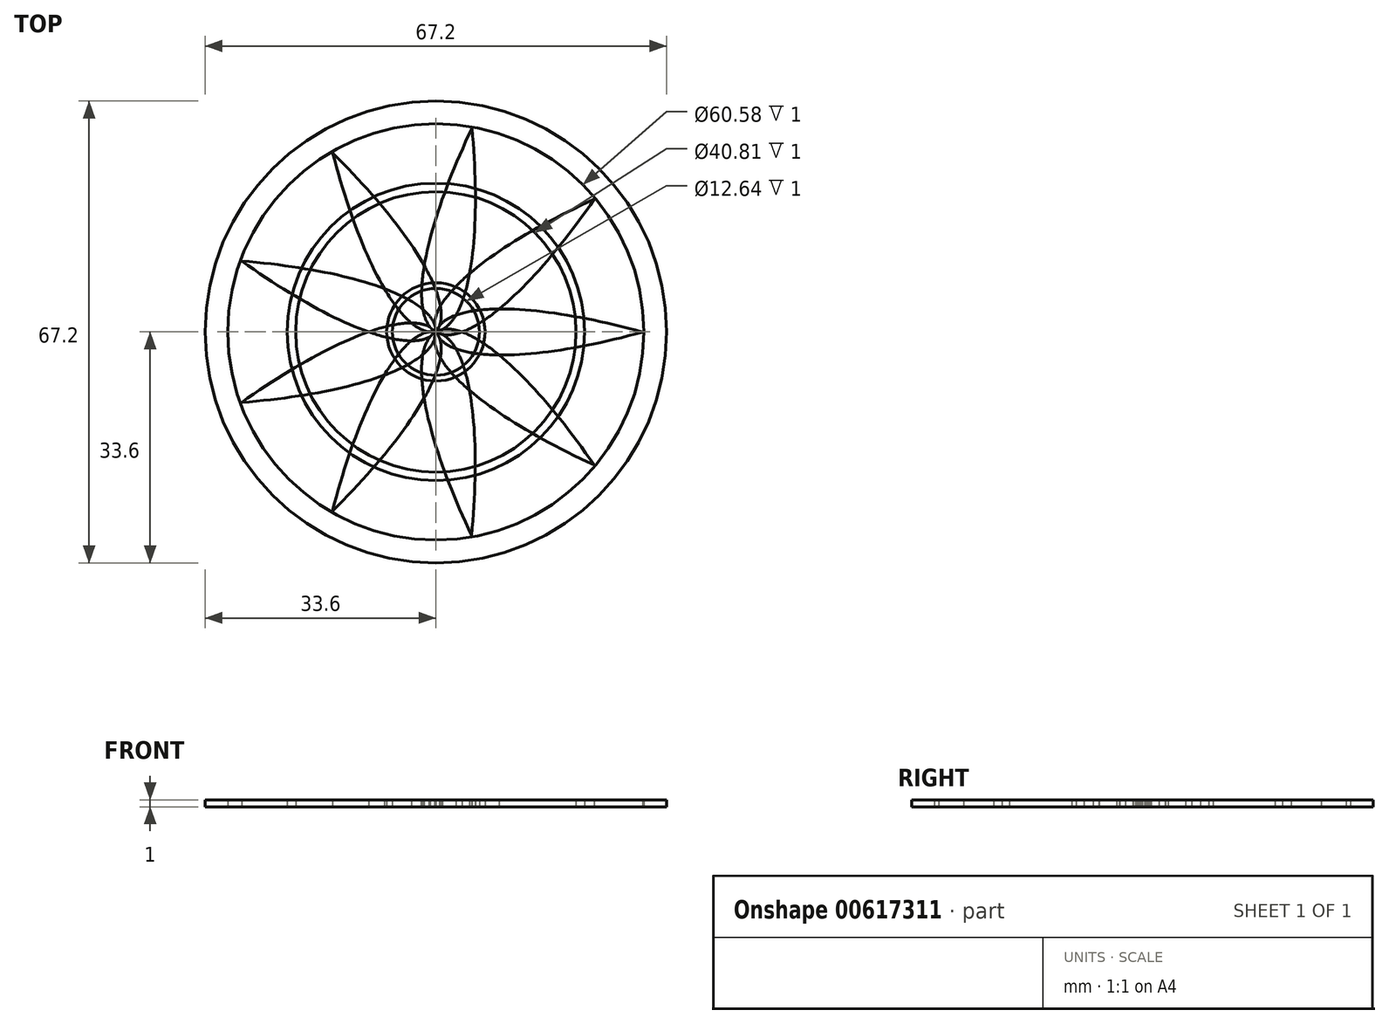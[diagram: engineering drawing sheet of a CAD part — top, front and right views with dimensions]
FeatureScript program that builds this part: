
annotation { "Feature Type Name" : "Feature", "Feature Type Description" : "" }
export const myFeature = defineFeature(function(context is Context, id is Id, definition is map)
    precondition{}
    {
        {
            var Q0;
            Q0=qCreatedBy(makeId("Top.planeOp"),FACE);
            var sketch = newSketch(context, id + "F0", { "sketchPlane" : qUnion([Q0])});
            skEllipse(sketch, "E0", {"center": v(-30.18, 25.36) * mm, "majorRadius": 39.42 * mm, "minorRadius": 10.73 * mm, "majorAxis": v(0.77, -0.64)});
            skEllipse(sketch, "E1.1.0", {"center": v(-39.42, 0.03) * mm, "majorRadius": 39.42 * mm, "minorRadius": 10.73 * mm, "majorAxis": v(1, 0)});
            skEllipse(sketch, "E1.2.0", {"center": v(-30.22, -25.31) * mm, "majorRadius": 39.42 * mm, "minorRadius": 10.73 * mm, "majorAxis": v(0.77, 0.64)});
            skEllipse(sketch, "E1.3.0", {"center": v(-6.88, -38.81) * mm, "majorRadius": 39.42 * mm, "minorRadius": 10.73 * mm, "majorAxis": v(0.17, 0.98)});
            skEllipse(sketch, "E1.4.0", {"center": v(19.68, -34.15) * mm, "majorRadius": 39.42 * mm, "minorRadius": 10.73 * mm, "majorAxis": v(-0.5, 0.87)});
            skEllipse(sketch, "E1.5.0", {"center": v(37.03, -13.51) * mm, "majorRadius": 39.42 * mm, "minorRadius": 10.73 * mm, "majorAxis": v(-0.94, 0.34)});
            skEllipse(sketch, "E1.6.0", {"center": v(37.05, 13.45) * mm, "majorRadius": 39.42 * mm, "minorRadius": 10.73 * mm, "majorAxis": v(-0.94, -0.34)});
            skEllipse(sketch, "E1.7.0", {"center": v(19.74, 34.12) * mm, "majorRadius": 39.42 * mm, "minorRadius": 10.73 * mm, "majorAxis": v(-0.5, -0.87)});
            skEllipse(sketch, "E1.8.0", {"center": v(-6.81, 38.82) * mm, "majorRadius": 39.42 * mm, "minorRadius": 10.73 * mm, "majorAxis": v(0.17, -0.98)});
            skPoint(sketch, "E1.center", {"position": v(0, 0) * mm});
            skSolve(sketch);
        }
        {
            var Q0;
            {var subQ0=sQuery(id+"F0.wireOp",EDGE,"E1.6.0");var subQ1=sQuery(id+"F0.wireOp",EDGE,"E1.1.0");var subQ2=makeQuery(id+"F0.imprint","INTERSECT",VERTEX,{"derivedFrom":[subQ1,subQ0]});Q0=makeQuery(id+"F0.imprint","IMPRINT",FACE,{"disambiguationData":[TD([[makeQuery(id+"F0.imprint","IMPRINT",EDGE,{"disambiguationData":[TD([[subQ2,-1.0]])],"derivedFrom":subQ1}),1.0]])]});}
            var Q1;
            {var subQ0=sQuery(id+"F0.wireOp",EDGE,"E1.5.0");var subQ1=sQuery(id+"F0.wireOp",EDGE,"E0");var subQ2=makeQuery(id+"F0.imprint","INTERSECT",VERTEX,{"derivedFrom":[subQ1,subQ0]});Q1=makeQuery(id+"F0.imprint","IMPRINT",FACE,{"disambiguationData":[TD([[makeQuery(id+"F0.imprint","IMPRINT",EDGE,{"disambiguationData":[TD([[subQ2,-1.0]])],"derivedFrom":subQ1}),1.0]])]});}
            var Q2;
            {var subQ0=sQuery(id+"F0.wireOp",EDGE,"E1.5.0");var subQ1=sQuery(id+"F0.wireOp",EDGE,"E0");var subQ2=makeQuery(id+"F0.imprint","INTERSECT",VERTEX,{"derivedFrom":[subQ1,subQ0]});Q2=makeQuery(id+"F0.imprint","IMPRINT",FACE,{"disambiguationData":[TD([[makeQuery(id+"F0.imprint","IMPRINT",EDGE,{"disambiguationData":[TD([[subQ2,1.0]])],"derivedFrom":subQ0}),1.0]])]});}
            var Q3;
            {var subQ0=sQuery(id+"F0.wireOp",EDGE,"E1.7.0");var subQ4=sQuery(id+"F0.wireOp",EDGE,"E1.4.0");var subQ6=makeQuery(id+"F0.imprint","INTERSECT",VERTEX,{"derivedFrom":[subQ4,subQ0]});Q3=makeQuery(id+"F0.imprint","IMPRINT",FACE,{"disambiguationData":[TD([[makeQuery(id+"F0.imprint","IMPRINT",EDGE,{"disambiguationData":[TD([[subQ6,-1.0]])],"derivedFrom":subQ4}),1.0]])]});}
            var Q4;
            {var subQ0=sQuery(id+"F0.wireOp",EDGE,"E1.6.0");var subQ4=sQuery(id+"F0.wireOp",EDGE,"E1.3.0");var subQ6=makeQuery(id+"F0.imprint","INTERSECT",VERTEX,{"derivedFrom":[subQ4,subQ0]});Q4=makeQuery(id+"F0.imprint","IMPRINT",FACE,{"disambiguationData":[TD([[makeQuery(id+"F0.imprint","IMPRINT",EDGE,{"disambiguationData":[TD([[subQ6,-1.0]])],"derivedFrom":subQ4}),1.0]])]});}
            var Q5;
            {var subQ0=sQuery(id+"F0.wireOp",EDGE,"E1.5.0");var subQ4=sQuery(id+"F0.wireOp",EDGE,"E1.2.0");var subQ6=makeQuery(id+"F0.imprint","INTERSECT",VERTEX,{"derivedFrom":[subQ4,subQ0]});Q5=makeQuery(id+"F0.imprint","IMPRINT",FACE,{"disambiguationData":[TD([[makeQuery(id+"F0.imprint","IMPRINT",EDGE,{"disambiguationData":[TD([[subQ6,-1.0]])],"derivedFrom":subQ4}),1.0]])]});}
            var Q6;
            {var subQ0=sQuery(id+"F0.wireOp",EDGE,"E1.4.0");var subQ4=sQuery(id+"F0.wireOp",EDGE,"E1.1.0");var subQ6=makeQuery(id+"F0.imprint","INTERSECT",VERTEX,{"derivedFrom":[subQ4,subQ0]});Q6=makeQuery(id+"F0.imprint","IMPRINT",FACE,{"disambiguationData":[TD([[makeQuery(id+"F0.imprint","IMPRINT",EDGE,{"disambiguationData":[TD([[subQ6,-1.0]])],"derivedFrom":subQ4}),1.0]])]});}
            var Q7;
            {var subQ0=sQuery(id+"F0.wireOp",EDGE,"E1.3.0");var subQ1=sQuery(id+"F0.wireOp",EDGE,"E0");var subQ2=makeQuery(id+"F0.imprint","INTERSECT",VERTEX,{"derivedFrom":[subQ1,subQ0]});Q7=makeQuery(id+"F0.imprint","IMPRINT",FACE,{"disambiguationData":[TD([[makeQuery(id+"F0.imprint","IMPRINT",EDGE,{"disambiguationData":[TD([[subQ2,-1.0]])],"derivedFrom":subQ1}),1.0]])]});}
            var Q8;
            {var subQ0=sQuery(id+"F0.wireOp",EDGE,"E1.7.0");var subQ1=sQuery(id+"F0.wireOp",EDGE,"E1.2.0");var subQ2=makeQuery(id+"F0.imprint","INTERSECT",VERTEX,{"derivedFrom":[subQ1,subQ0]});Q8=makeQuery(id+"F0.imprint","IMPRINT",FACE,{"disambiguationData":[TD([[makeQuery(id+"F0.imprint","IMPRINT",EDGE,{"disambiguationData":[TD([[subQ2,-1.0]])],"derivedFrom":subQ1}),1.0]])]});}
            extrude(context, id + "F1", {"entities" : qUnion([Q0, Q1, Q2, Q3, Q4, Q5, Q6, Q7, Q8]), "depth" : 1 * mm, "offsetDistance" : 25 * mm});
        }
        {
            var Q0;
            {var subQ0=sQuery(id+"F0.wireOp",EDGE,"E1.8.0");var subQ1=sQuery(id+"F0.wireOp",EDGE,"E0");var subQ2=makeQuery(id+"F0.imprint","INTERSECT",VERTEX,{"derivedFrom":[subQ1,subQ0]});Q0=makeQuery(id+"F0.imprint","IMPRINT",FACE,{"disambiguationData":[TD([[makeQuery(id+"F0.imprint","IMPRINT",EDGE,{"disambiguationData":[TD([[subQ2,1.0]])],"derivedFrom":subQ1}),1.0]])]});}
            var Q1;
            {var subQ0=sQuery(id+"F0.wireOp",EDGE,"E1.6.0");var subQ1=sQuery(id+"F0.wireOp",EDGE,"E0");var subQ2=makeQuery(id+"F0.imprint","INTERSECT",VERTEX,{"derivedFrom":[subQ1,subQ0]});Q1=makeQuery(id+"F0.imprint","IMPRINT",FACE,{"disambiguationData":[TD([[makeQuery(id+"F0.imprint","IMPRINT",EDGE,{"disambiguationData":[TD([[subQ2,-1.0]])],"derivedFrom":subQ1}),-1.0]])]});}
            var Q2;
            {var subQ0=sQuery(id+"F0.wireOp",EDGE,"E1.7.0");var subQ1=sQuery(id+"F0.wireOp",EDGE,"E1.5.0");var subQ2=makeQuery(id+"F0.imprint","INTERSECT",VERTEX,{"derivedFrom":[subQ1,subQ0]});Q2=makeQuery(id+"F0.imprint","IMPRINT",FACE,{"disambiguationData":[TD([[makeQuery(id+"F0.imprint","IMPRINT",EDGE,{"disambiguationData":[TD([[subQ2,-1.0]])],"derivedFrom":subQ1}),-1.0]])]});}
            var Q3;
            {var subQ0=sQuery(id+"F0.wireOp",EDGE,"E1.6.0");var subQ1=sQuery(id+"F0.wireOp",EDGE,"E1.4.0");var subQ2=makeQuery(id+"F0.imprint","INTERSECT",VERTEX,{"derivedFrom":[subQ1,subQ0]});Q3=makeQuery(id+"F0.imprint","IMPRINT",FACE,{"disambiguationData":[TD([[makeQuery(id+"F0.imprint","IMPRINT",EDGE,{"disambiguationData":[TD([[subQ2,-1.0]])],"derivedFrom":subQ1}),-1.0]])]});}
            var Q4;
            {var subQ0=sQuery(id+"F0.wireOp",EDGE,"E1.5.0");var subQ1=sQuery(id+"F0.wireOp",EDGE,"E1.3.0");var subQ2=makeQuery(id+"F0.imprint","INTERSECT",VERTEX,{"derivedFrom":[subQ1,subQ0]});Q4=makeQuery(id+"F0.imprint","IMPRINT",FACE,{"disambiguationData":[TD([[makeQuery(id+"F0.imprint","IMPRINT",EDGE,{"disambiguationData":[TD([[subQ2,-1.0]])],"derivedFrom":subQ1}),-1.0]])]});}
            var Q5;
            {var subQ0=sQuery(id+"F0.wireOp",EDGE,"E1.4.0");var subQ1=sQuery(id+"F0.wireOp",EDGE,"E1.2.0");var subQ2=makeQuery(id+"F0.imprint","INTERSECT",VERTEX,{"derivedFrom":[subQ1,subQ0]});Q5=makeQuery(id+"F0.imprint","IMPRINT",FACE,{"disambiguationData":[TD([[makeQuery(id+"F0.imprint","IMPRINT",EDGE,{"disambiguationData":[TD([[subQ2,-1.0]])],"derivedFrom":subQ1}),-1.0]])]});}
            var Q6;
            {var subQ0=sQuery(id+"F0.wireOp",EDGE,"E1.3.0");var subQ1=sQuery(id+"F0.wireOp",EDGE,"E1.1.0");var subQ2=makeQuery(id+"F0.imprint","INTERSECT",VERTEX,{"derivedFrom":[subQ1,subQ0]});Q6=makeQuery(id+"F0.imprint","IMPRINT",FACE,{"disambiguationData":[TD([[makeQuery(id+"F0.imprint","IMPRINT",EDGE,{"disambiguationData":[TD([[subQ2,-1.0]])],"derivedFrom":subQ1}),-1.0]])]});}
            var Q7;
            {var subQ0=sQuery(id+"F0.wireOp",EDGE,"E1.2.0");var subQ1=sQuery(id+"F0.wireOp",EDGE,"E0");var subQ2=makeQuery(id+"F0.imprint","INTERSECT",VERTEX,{"derivedFrom":[subQ1,subQ0]});Q7=makeQuery(id+"F0.imprint","IMPRINT",FACE,{"disambiguationData":[TD([[makeQuery(id+"F0.imprint","IMPRINT",EDGE,{"disambiguationData":[TD([[subQ2,-1.0]])],"derivedFrom":subQ1}),-1.0]])]});}
            var Q8;
            {var subQ0=sQuery(id+"F0.wireOp",EDGE,"E1.1.0");var subQ1=sQuery(id+"F0.wireOp",EDGE,"E0");var subQ2=makeQuery(id+"F0.imprint","INTERSECT",VERTEX,{"derivedFrom":[subQ1,subQ0]});Q8=makeQuery(id+"F0.imprint","IMPRINT",FACE,{"disambiguationData":[TD([[makeQuery(id+"F0.imprint","IMPRINT",EDGE,{"disambiguationData":[TD([[subQ2,-1.0]])],"derivedFrom":subQ1}),1.0]])]});}
            extrude(context, id + "F2", {"entities" : qUnion([Q0, Q1, Q2, Q3, Q4, Q5, Q6, Q7, Q8]), "depth" : 1 * mm, "offsetDistance" : 25 * mm});
        }
        {
            var Q0;
            Q0=qCreatedBy(makeId("Top.planeOp"),FACE);
            var sketch = newSketch(context, id + "F3", { "sketchPlane" : qUnion([Q0])});
            skCircle(sketch, "E2", {"center": v(0, 0) * mm, "radius": 30.29 * mm});
            skCircle(sketch, "E3", {"center": v(0, 0) * mm, "radius": 33.6 * mm});
            skSolve(sketch);
        }
        {
            var Q0;
            Q0 = qSketchRegion(id + "F3", true);
            extrude(context, id + "F4", {"entities" : qUnion([Q0]), "depth" : 1 * mm, "offsetDistance" : 25 * mm});
        }
        {
            var Q0;
            {var subQ0=sQuery(id+"F0.wireOp",EDGE,"E1.2.0");var subQ1=sQuery(id+"F0.wireOp",EDGE,"E1.1.0");var subQ2=makeQuery(id+"F0.imprint","INTERSECT",VERTEX,{"derivedFrom":[subQ1,subQ0]});Q0=makeQuery(id+"F0.imprint","IMPRINT",FACE,{"disambiguationData":[TD([[makeQuery(id+"F0.imprint","IMPRINT",EDGE,{"disambiguationData":[TD([[subQ2,-1.0]])],"derivedFrom":subQ1}),-1.0]])]});}
            var sketch = newSketch(context, id + "F5", { "sketchPlane" : qUnion([Q0])});
            skCircle(sketch, "E4", {"center": v(0, 0) * mm, "radius": 2.47 * mm});
            skCircle(sketch, "E5", {"center": v(0, 0) * mm, "radius": 3.2 * mm});
            skSolve(sketch);
        }
        {
            var Q0;
            Q0=sQuery(id+"F5.wireOp",EDGE,"E4");
            var Q1;
            Q1=sQuery(id+"F5.wireOp",EDGE,"E5");
            extrude(context, id + "F6", {"bodyType" : ToolBodyType.SURFACE, "surfaceEntities" : qUnion([Q0, Q1]), "depth" : 1 * mm, "offsetDistance" : 25 * mm});
        }
        {
            var Q0;
            Q0=makeQuery(id+"F3.imprint","IMPRINT",FACE,{"disambiguationData":[TD([[makeQuery(id+"F3.imprint","IMPRINT",EDGE,{"derivedFrom":sQuery(id+"F3.wireOp",EDGE,"E2")}),1.0]])]});
            var sketch = newSketch(context, id + "F7", { "sketchPlane" : qUnion([Q0])});
            skCircle(sketch, "E6", {"center": v(0, 0) * mm, "radius": 6.32 * mm});
            skCircle(sketch, "E7", {"center": v(0, 0) * mm, "radius": 7.15 * mm});
            skSolve(sketch);
        }
        {
            var Q0;
            Q0 = qSketchRegion(id + "F7", true);
            extrude(context, id + "F8", {"entities" : qUnion([Q0]), "depth" : 1 * mm, "offsetDistance" : 25 * mm});
        }
        {
            var Q0;
            Q0=makeQuery(id+"F3.imprint","IMPRINT",FACE,{"disambiguationData":[TD([[makeQuery(id+"F3.imprint","IMPRINT",EDGE,{"derivedFrom":sQuery(id+"F3.wireOp",EDGE,"E2")}),1.0]])]});
            var sketch = newSketch(context, id + "F9", { "sketchPlane" : qUnion([Q0])});
            skCircle(sketch, "E8", {"center": v(0, 0) * mm, "radius": 20.4 * mm});
            skCircle(sketch, "E9", {"center": v(0, 0) * mm, "radius": 21.64 * mm});
            skSolve(sketch);
        }
        {
            var Q0;
            Q0 = qSketchRegion(id + "F9", true);
            extrude(context, id + "F10", {"entities" : qUnion([Q0]), "depth" : 1 * mm, "offsetDistance" : 25 * mm});
        }
    });
